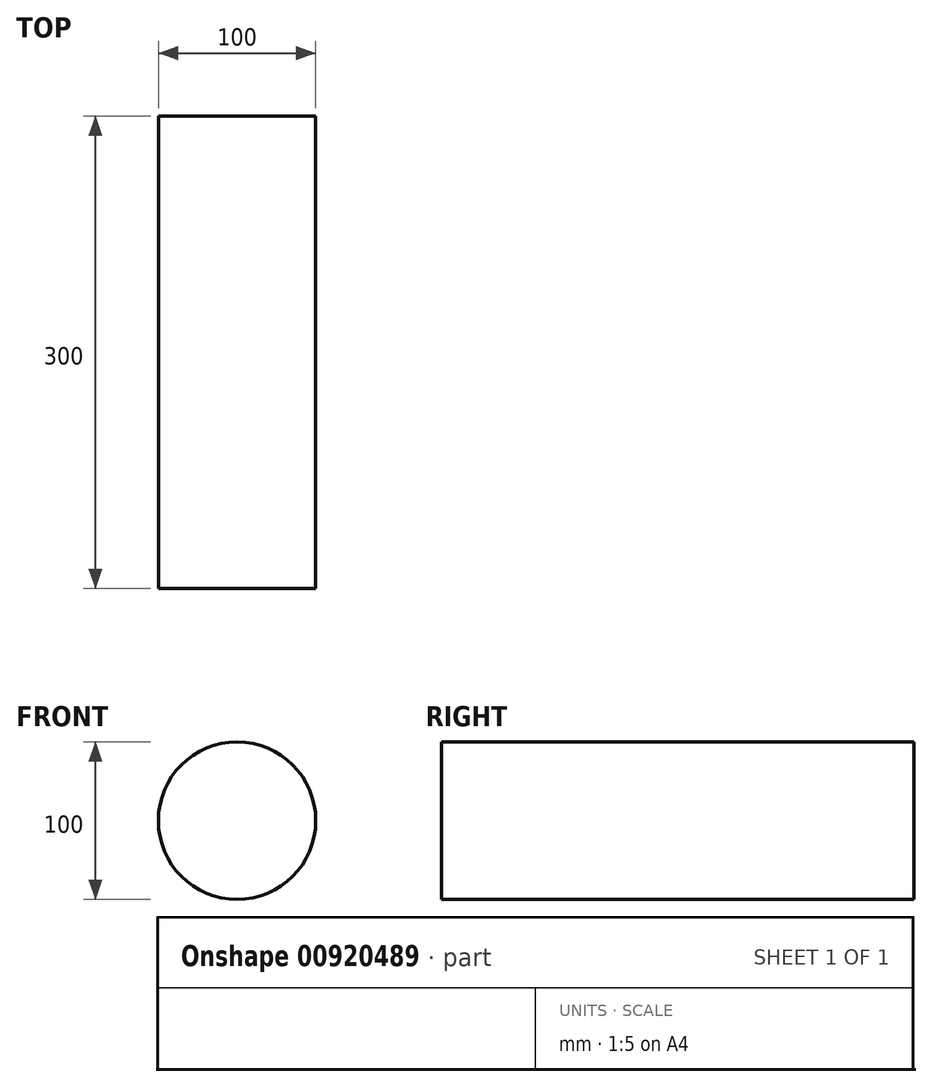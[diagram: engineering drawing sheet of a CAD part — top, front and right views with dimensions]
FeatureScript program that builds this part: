
annotation { "Feature Type Name" : "Feature", "Feature Type Description" : "" }
export const myFeature = defineFeature(function(context is Context, id is Id, definition is map)
    precondition{}
    {
        {
            var Q0;
            Q0=qCreatedBy(makeId("Front.planeOp"),FACE);
            var sketch = newSketch(context, id + "F0", { "sketchPlane" : qUnion([Q0])});
            skCircle(sketch, "E0", {"center": v(0, -2.66) * mm, "radius": 50 * mm});
            skSolve(sketch);
        }
        {
            var Q0;
            Q0=makeQuery(id+"F0.imprint","IMPRINT",FACE,{"disambiguationData":[TD([[makeQuery(id+"F0.imprint","IMPRINT",EDGE,{"derivedFrom":sQuery(id+"F0.wireOp",EDGE,"E0")}),1.0]])]});
            extrude(context, id + "F1", {"entities" : qUnion([Q0]), "depth" : 300 * mm, "offsetDistance" : 25 * mm});
        }
    });
